# Revit family: Legrand Plexo³ multifunction sleeve
name_source: partatom
category: Equipement électrique
revit_build: Autodesk Revit 2018 (Build: 20170223_1515(x64)
units: mm (PartAtom-declared; Revit-internal decimal feet)

## family parameters
Basée sur le plan de construction = Non
Configuration du panneau = Deux colonnes, circuits au sein
Cote de connecteur circulaire = Utiliser le diamètre
Couper avec des vides une fois chargée = Non
Numéro OmniClass = 23.80.30.11.17
Partagée = Non
Point de calcul de pièce = Non
Titre OmniClass = Distribution Boards and Control Panels
Toujours verticalement = Oui
Type d'élément = Tableau de raccordement

## types (2) — shared parameters
ETIM Class 6.0 = EC000214
Fabricant = Legrand
General Conditions of Use = https://export.legrand.com
IK = 09
IP = 65
Image du type = <Aucun>
Material = Polystyrene
Polystyrene
RAL = 7046
URL = www.legrand.fr

## per-type parameters (varying)
| type | Description | Multifunction sleeve 001917 | Multifunction sleeve 001918 |
| Legrand Plexo³ multifunction sleeve 3 rows | Legrand Plexo³ multifunction sleeve 3 rows 001918 | Non | Oui |
| Legrand Plexo³ multifunction sleeve 2 rows | Legrand Plexo³ multifunction sleeve 2 rows 001917 | Oui | Non |
